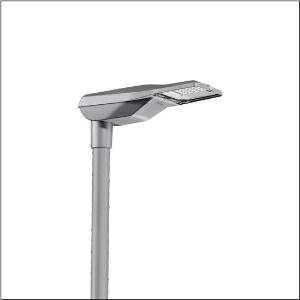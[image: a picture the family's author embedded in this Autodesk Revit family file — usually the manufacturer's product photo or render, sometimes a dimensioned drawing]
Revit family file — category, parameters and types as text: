
# Revit family: streetlight_sl_21_iq_micro___st0_8a_5xe1c31g08cb_6ed2
name_source: partatom
category: Lighting Fixtures
units: mm (PartAtom-declared; Revit-internal decimal feet)

## family parameters
Cut with Voids When Loaded = No
Host = Face
Light Source = No
Part Type = Normal
Room Calculation Point = No
Round Connector Dimension = Use Diameter
Shared = No

## types (1)
- --- (1 x LED, 2870 lm, 19.4 W, 3000K)
    Apparent Load = 19 VA
    CIE Flux Codes = 38 75 97 100 100
    Color Rendering = 70
    Color Temperature = 3000K
    Default Elevation = 1800 mm
    Description = Streetlight SL 21 iQ micro, mast luminaire, primary light control with lens, of PMMA, primary optical cover: cover, of toughened safety glass, transparent, light distribution: ST0.8a, light emission: direct distribution, primary light characteristic: asymmetric, installation type: post-top, side-entry, LED, High Power LED, rated luminous flux: 2.870lm, luminous efficacy: 148lm/W, light colour: 730, colour temperature: 3000K, control: Street-Remote, Auto-Match, Temp-Guard, Lumen-Switch, Night-Set, Smart-Wire, Light-Fading, Desk-Remote (wireless, voltage-free reading and setting of iQ features in the workshop via application-optimized NFC function/RFID function), optimised constant luminous flux control (CLO 2.0), pre-setting: linear dimming characteristic, mains connection: 220..240V, AC, 50/60Hz, start of lifetime: 19W, end of service life: 20W, reduction: 10W, luminaire housing, of diecast aluminium, powder-coated, Siteco® metallic grey (DB 702S), corrosivity category C5 mid according to DIN EN ISO 12944, please order mast flange separately, inclination adjustable: 0°, 5°, 10°, 15°, sealing non-destructively replaceable, multi-level sealing system, length: 528mm, width: 235mm, height: 110mm, mast flange for spigot size: 42mm (side-entry): 5XC10008XM4, 60/48mm (side-entry/post-top): 5XC10108XM2, 76/60mm (side-entry/post-top): 5XC10108XM1, protection rating (complete): IP66, insulation class (complete): insulation class II (safety insulation), certification: CE, ENEC, ENEC+, VDE, impact resistance: IK09, permissible operating ambient temperature for outdoor applications: -40..+50°C, standard-compliant lighting for roads and squares, packaging unit: 1 piece

Light Distribution: ST0.8a
    Height = 110 mm
    Lamp = 1 x LED
    Lamp Light Flux = 2870 lm
    Lamp Power = 19.4 W
    Lamp count = 1
    Length = 528 mm
    Luminous efficacy = 148 lm/W
    Manufacturer = Siteco
    ModVariant = No
    Model = 5XE1C31G08CB
    Number of Poles = 1
    OnlyDefault = Yes
    Power Factor = 1
    Product Name = Streetlight SL 21 iQ micro | ST0.8a
    Product group = mast luminaire | pylon top
    ProductGroupID = 6100
    Protection Class = Protection class II
    Protection Degree = IP 66
    RLX_Detail_Level = 1
    RLX_Emergency_Light_Flux = 0 lm
    RLX_Emergency_Type = 0
    RLX_Emergency_Type_DB = No
    RlxData = <blob elided: 98809 chars, md5=b1dcdd07>
    Socket = socket
    Standby Power = 0 W
    System Light Flux = 2870 lm
    System Power = 19 W
    Type Comments = factory setting: luminous flux: 100 % | dim-lin: 254 | 387 mA
    Type Image = l_1006881.jpg
    URL = http://relux.com
    VarID = @adj_108231
    Voltage = 0 V
    Weight = 0.00 kg
    Width = 235 mm

## geometry (parser evidence)
native form markers: Blend x4, Sweep x12
no freeform markers — native parametric forms only
